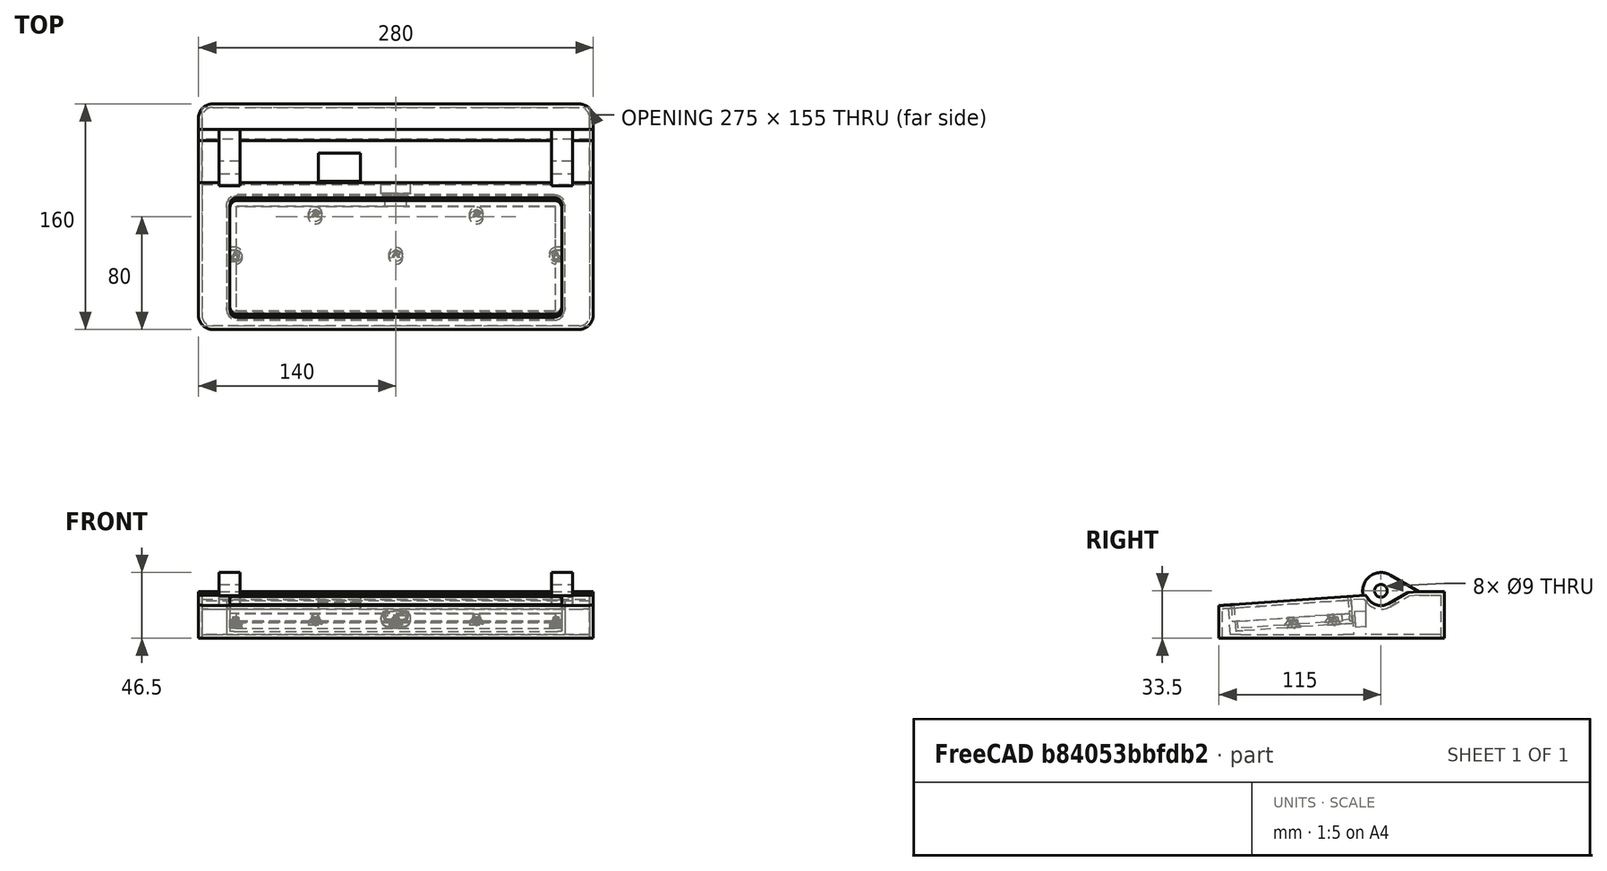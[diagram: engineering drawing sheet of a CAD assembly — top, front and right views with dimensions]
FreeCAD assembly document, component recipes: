
FREECAD ASSEMBLY — COMPONENT RECIPES ("BottomEnclosure_v3")

This assembly document has 6 components, labeled P0..P5 below (a component is one placed body or linked part). 5 of them carry a construction recipe — the FreeCAD feature program that regenerates the part from scratch, quoted from this document or its linked companion documents; the rest are supplied as boundary geometry only. No exploded tour is included for this assembly.
COMPONENT P0 — recipe-attached ("Bottom Enclosure - 0", modeled in this document).
Construction recipe (the document's own serialized feature program — sketch geometry with constraints, then the solid features built on it; lengths are millimeters unless a unit is written):

FEATURE [PartDesign::Boolean] Boolean
  Group = -> [Binder]
  Refine = true
  Suppressed = false
  Type = 0
  UsePlacement = true
FEATURE [PartDesign::SubShapeBinder] Binder011
  BindCopyOnChange = 0
  BindMode = 0
  ClaimChildren = false
  Context = -> Body [Binder011.]
  Fuse = false
  MakeFace = false
  OffsetFill = false
  OffsetIntersection = false
  OffsetJoinType = 0
  OffsetOpenResult = false
  PartialLoad = false
  Placement = pos=(-3.64e-14,-49.9267,26.5088) rot=(1,0,0;0.069813rad)
  Refine = true
  Relative = true
  Support = -> [Link001,Link002]
  _Version = 2
  expr: .Placement.Rotation.Angle = <<Vars>>.hood_angle
FEATURE [PartDesign::SubShapeBinder] Binder018
  BindCopyOnChange = 0
  BindMode = 0
  ClaimChildren = false
  Context = -> Body [Binder018.]
  Fuse = false
  MakeFace = true
  Offset = 2.5
  OffsetFill = false
  OffsetIntersection = false
  OffsetJoinType = 2
  OffsetOpenResult = false
  PartialLoad = false
  Refine = true
  Relative = true
  Support = -> [Binder011[Edge14,Edge13,Edge12,Edge11,Edge7,Edge8,Edge9,Edge10]]
  _Version = 2
  expr: Offset = <<Vars>>.wall
FEATURE [PartDesign::Pad] Pad
  BaseFeature = -> Boolean
  Direction = (0,-0.0697565,0.997564)
  Length = 10
  Length2 = 10
  Offset = -2.5
  Profile = -> Binder018
  Refine = true
  Suppressed = false
  Type = 3
  UpToFace = -> Boolean [Face12]
  expr: Offset = -<<Vars>>.wall
FEATURE [PartDesign::SubShapeBinder] Binder019
  BindCopyOnChange = 0
  BindMode = 0
  ClaimChildren = false
  Context = -> Body [Binder019.]
  Fuse = false
  MakeFace = true
  Offset = 0.2
  OffsetFill = false
  OffsetIntersection = false
  OffsetJoinType = 2
  OffsetOpenResult = false
  PartialLoad = false
  Refine = true
  Relative = true
  Support = -> [Binder011[Edge7,Edge14,Edge13,Edge12,Edge11,Edge10,Edge9,Edge8]]
  _Version = 2
  expr: Offset = <<Vars>>.clearance
FEATURE [PartDesign::Pocket] Pocket
  BaseFeature = -> Pad
  Direction = (0,0.0697565,-0.997564)
  Length = 12
  Length2 = 5
  Profile = -> Binder019
  Refine = true
  Suppressed = false
  Type = 0
FEATURE [PartDesign::SubShapeBinder] Binder020
  BindCopyOnChange = 0
  BindMode = 0
  ClaimChildren = false
  Context = -> Body [Binder020.]
  Fuse = false
  MakeFace = true
  Offset = -1
  OffsetFill = false
  OffsetIntersection = false
  OffsetJoinType = 0
  OffsetOpenResult = false
  PartialLoad = false
  Placement = pos=(0,0,-12) rot=(0,0,1;0rad)
  Refine = true
  Relative = true
  Support = -> [Binder011[Edge16,Edge15,Edge18,Edge17]]
  _Version = 2
FEATURE [PartDesign::Pocket] Pocket005
  BaseFeature = -> Pocket
  Direction = (0,0.0697565,-0.997564)
  Length = 5
  Length2 = 5
  Profile = -> Binder020
  Refine = true
  Suppressed = false
  Type = 0
FEATURE [Sketcher::SketchObject] Sketch014  label="Sketch015"
  ArcFitTolerance = 1e-06
  AttachmentSupport = -> [Pocket005]
  ExternalGeometry = -> [Binder011]
  FullyConstrained = true
  MakeInternals = false
  MapMode = 5
  Placement = pos=(0,-0.903776,12.9246) rot=(1,0,0;0.069813rad)
  sketch-geometry (5):
    g0: Circle CenterX=-113.798 CenterY=-47.9567 CenterZ=0 NormalX=0 NormalY=0 NormalZ=1 AngleXU=0 Radius=2.5
    g1: Circle CenterX=-57.1492 CenterY=-19.3809 CenterZ=0 NormalX=0 NormalY=0 NormalZ=1 AngleXU=0 Radius=2.5
    g2: Circle CenterX=-3.64e-14 CenterY=-47.9559 CenterZ=0 NormalX=0 NormalY=0 NormalZ=1 AngleXU=0 Radius=2.5
    g3: Circle CenterX=57.151 CenterY=-19.3809 CenterZ=0 NormalX=0 NormalY=0 NormalZ=1 AngleXU=0 Radius=2.5
    g4: Circle CenterX=113.801 CenterY=-47.9567 CenterZ=0 NormalX=0 NormalY=0 NormalZ=1 AngleXU=0 Radius=2.5
  constraints (10):
    c: Coincident(g0,g-4)
    c: Coincident(g1,g-3)
    c: Coincident(g2,g-5)
    c: Coincident(g3,g-6)
    c: Coincident(g4,g-7)
    c: Equal(g4,g3)
    c: Equal(g3,g2)
    c: Equal(g2,g1)
    c: Equal(g1,g0)
    c: Diameter(g2) = 5
FEATURE [PartDesign::Pad] Pad003
  BaseFeature = -> Pocket005
  Direction = (0,-0.0697565,0.997564)
  Length = 5
  Length2 = 10
  Profile = -> Sketch014
  ReferenceAxis = -> Sketch014 [N_Axis]
  Refine = true
  Suppressed = false
  Type = 0
FEATURE [PartDesign::Chamfer] Chamfer
  Angle = 45
  Base = -> Pad003 [Edge215,Edge233,Edge232,Edge231,Edge225]
  BaseFeature = -> Pad003
  ChamferType = 0
  FlipDirection = false
  Refine = true
  Size = 2.5
  Size2 = 1
  SupportTransform = false
  Suppressed = false
  UseAllEdges = false
FEATURE [PartDesign::Hole] Hole
  BaseFeature = -> Chamfer
  CustomThreadClearance = 0
  Depth = 4
  DepthType = 0
  Diameter = 3
  DrillForDepth = false
  DrillPoint = 1
  DrillPointAngle = 118
  HoleCutCountersinkAngle = 90
  HoleCutCustomValues = false
  HoleCutDepth = 0
  HoleCutDiameter = 6.1
  HoleCutType = 0
  ModelThread = false
  Profile = -> Chamfer [Edge10,Edge87,Edge89,Edge91,Edge64]
  Refine = true
  Suppressed = false
  Tapered = false
  TaperedAngle = 90
  ThreadClass = 0
  ThreadDepth = 4
  ThreadDepthType = 0
  ThreadDirection = 0
  ThreadFit = 0
  ThreadSize = 0
  ThreadType = 0
  Threaded = false
  UseCustomThreadClearance = false
  expr: Diameter = <<Vars>>.nut_inserts_m2
FEATURE [Sketcher::SketchObject] Sketch015  label="Sketch016"
  ArcFitTolerance = 1e-06
  AttachmentSupport = -> [Hole]
  ExternalGeometry = -> [Hole]
  FullyConstrained = true
  MakeInternals = false
  MapMode = 5
  Placement = pos=(0,-6.49004,-0.453828) rot=(1,0,0;1.64061rad)
  sketch-geometry (8):
    g0: LineSegment StartX=-7.5 StartY=17.9269 StartZ=0 EndX=-7.5 EndY=15.9269 EndZ=0
    g1: LineSegment StartX=-5.5 StartY=13.9269 StartZ=0 EndX=5.5 EndY=13.9269 EndZ=0
    g2: LineSegment StartX=7.5 StartY=15.9269 StartZ=0 EndX=7.5 EndY=17.9269 EndZ=0
    g3: LineSegment StartX=7.5 StartY=17.9269 StartZ=0 EndX=-7.5 EndY=17.9269 EndZ=0
    g4: ArcOfCircle CenterX=-5.5 CenterY=15.9269 CenterZ=0 NormalX=0 NormalY=0 NormalZ=1 AngleXU=0 Radius=2 StartAngle=3.14159 EndAngle=4.71239
    g5: GeomPoint [constr] X=-7.5 Y=13.9269 Z=0
    g6: ArcOfCircle CenterX=5.5 CenterY=15.9269 CenterZ=0 NormalX=0 NormalY=0 NormalZ=1 AngleXU=0 Radius=2 StartAngle=4.71239 EndAngle=6.28319
    g7: GeomPoint [constr] X=7.5 Y=13.9269 Z=0
  constraints (19):
    c: Coincident(g2,g3)
    c: Coincident(g3,g0)
    c: Vertical(g0)
    c: Vertical(g2)
    c: Horizontal(g1)
    c: Symmetric(g0,g2,g-2)
    c: DistanceX(g3,g3) = 15
    c: DistanceY(g7,g2) = 4
    c: PointOnObject(g0,g-3)
    c: PointOnObject(g5,g0)
    c: PointOnObject(g5,g1)
    c: Tangent(g0,g4) = -1.5708
    c: Tangent(g1,g4) = -1.5708
    c: PointOnObject(g7,g1)
    c: PointOnObject(g7,g2)
    c: Tangent(g1,g6) = -1.5708
    c: Tangent(g2,g6) = -1.5708
    c: Equal(g6,g4)
    c: Radius(g6) = 2
FEATURE [PartDesign::Pocket] Pocket006
  BaseFeature = -> Hole
  Direction = (0,0.997564,0.0697565)
  Length = 20
  Length2 = 5
  Midplane = true
  Profile = -> Sketch015
  ReferenceAxis = -> Sketch015 [N_Axis]
  Refine = true
  Suppressed = false
  Type = 0
FEATURE [PartDesign::SubShapeBinder] Binder021
  BindCopyOnChange = 0
  BindMode = 0
  ClaimChildren = false
  Context = -> Body [Binder021.]
  Fuse = false
  MakeFace = true
  Offset = 1.5
  OffsetFill = false
  OffsetIntersection = false
  OffsetJoinType = 2
  OffsetOpenResult = false
  PartialLoad = false
  Refine = true
  Relative = true
  Support = -> [Pocket006[Edge110,Edge69,Edge93,Edge91,Edge89,Edge80]]
  _Version = 2
FEATURE [PartDesign::Pocket] Pocket007
  BaseFeature = -> Pocket006
  Direction = (0,-0.997564,-0.0697565)
  Length = 2
  Length2 = 5
  Profile = -> Binder021
  Refine = true
  Suppressed = false
  Type = 0
FEATURE [PartDesign::Body] Body  label="Bottom Enclosure - 0"
  AllowCompound = false
  Group = -> [Boolean,Binder011,Binder018,Pad,Binder019,Pocket,Binder020,Pocket005,Sketch014,Pad003,Chamfer,Hole,Sketch015,Pocket006,Binder021,Pocket007]
  Origin = -> Origin
  Tip = -> Pocket007
COMPONENT P1 — recipe-attached ("Bottom Enclosure - Base", modeled in this document).
Construction recipe (the document's own serialized feature program — sketch geometry with constraints, then the solid features built on it; lengths are millimeters unless a unit is written):

FEATURE [Sketcher::SketchObject] Sketch008
  ArcFitTolerance = 1e-06
  AttachmentSupport = -> [YZ_Plane002]
  FullyConstrained = true
  MakeInternals = false
  MapMode = 5
  Placement = pos=(0,0,0) rot=(0.57735,0.57735,0.57735;2.0944rad)
  expr: Constraints[15] = <<Vars>>.hood_angle
  expr: Constraints[16] = <<Vars>>.bottom_enclosure_height
  expr: Constraints[8] = <<Vars>>.top_enclosure_height
  expr: Constraints[9] = <<Vars>>.bottom_enclosure_depth
  sketch-geometry (12):
    g0: LineSegment StartX=-100 StartY=0 StartZ=0 EndX=-100 EndY=23.0073 EndZ=0
    g1: LineSegment StartX=-100 StartY=23.0073 StartZ=0 EndX=0 EndY=30 EndZ=0
    g2: LineSegment StartX=60 StartY=32.9354 StartZ=0 EndX=60 EndY=0 EndZ=0
    g3: LineSegment StartX=60 StartY=0 StartZ=0 EndX=-100 EndY=0 EndZ=0
    g4: LineSegment [constr] StartX=0 StartY=30 StartZ=0 EndX=-100 EndY=30 EndZ=0
    g5: LineSegment [constr] StartX=-100 StartY=30 StartZ=0 EndX=-100 EndY=23.0073 EndZ=0
    g6: LineSegment [constr] StartX=41.9779 StartY=32.9354 StartZ=0 EndX=21.5 EndY=44.7583 EndZ=0
    g7: LineSegment StartX=0 StartY=30 StartZ=0 EndX=41.9779 EndY=32.9354 EndZ=0
    g8: LineSegment StartX=41.9779 StartY=32.9354 StartZ=0 EndX=60 EndY=32.9354 EndZ=0
    g9: Circle CenterX=15 CenterY=33.5 CenterZ=0 NormalX=0 NormalY=0 NormalZ=1 AngleXU=0 Radius=4.5
    g10: Circle CenterX=15 CenterY=33.5 CenterZ=0 NormalX=0 NormalY=0 NormalZ=1 AngleXU=0 Radius=10
    g11: LineSegment [constr] StartX=15 StartY=33.5 StartZ=0 EndX=21.5 EndY=44.7583 EndZ=0
  constraints (33):
    c: PointOnObject(g0,g-1)
    c: Vertical(g0)
    c: Coincident(g0,g1)
    c: PointOnObject(g1,g-2)
    c: PointOnObject(g2,g-1)
    c: Vertical(g2)
    c: Coincident(g2,g3)
    c: Coincident(g3,g0)
    c: DistanceX(g0,g-1) = 100
    c: DistanceY(g0,g1) = 30
    c: Coincident(g1,g4)
    c: Horizontal(g4)
    c: Coincident(g4,g5)
    c: Coincident(g5,g0)
    c: Vertical(g5)
    c: Angle(g4,g1) = 0.0698132
    c: DistanceX(g0,g2) = 160
    c: Angle(g6,g-1) = 0.523599
    c: Coincident(g7,g1)
    c: Coincident(g7,g6)
    c: Coincident(g8,g6)
    c: Coincident(g8,g2)
    c: Horizontal(g8)
    c: Parallel(g1,g7)
    c: DistanceX(g-1,g9) = 15
    c: Diameter(g9) = 9
    c: DistanceY(g-1,g9) = 33.5
    c: Coincident(g10,g9)
    c: Diameter(g10) = 20
    c: Coincident(g11,g9)
    c: Coincident(g6,g11)
    c: Perpendicular(g6,g11)
    c: Distance(g11) = 13
FEATURE [Sketcher::SketchObject] Sketch
  ArcFitTolerance = 1e-06
  AttachmentSupport = -> [YZ_Plane002]
  ExternalGeometry = -> [Sketch008]
  FullyConstrained = true
  MakeInternals = false
  MapMode = 5
  Placement = pos=(0,0,0) rot=(0.57735,0.57735,0.57735;2.0944rad)
  sketch-geometry (6):
    g0: ArcOfCircle CenterX=15 CenterY=33.5 CenterZ=0 NormalX=0 NormalY=0 NormalZ=1 AngleXU=0 Radius=10.5 StartAngle=3.83972 EndAngle=5.23599
    g1: LineSegment StartX=3.99563 StartY=30.2794 StartZ=0 EndX=6.95653 EndY=26.7507 EndZ=0
    g2: LineSegment StartX=20.25 StartY=24.4067 StartZ=0 EndX=34.0635 EndY=32.382 EndZ=0
    g3: LineSegment [constr] StartX=6.95653 StartY=26.7507 StartZ=0 EndX=7.33956 EndY=27.0721 EndZ=0
    g4: LineSegment [constr] StartX=7.33956 StartY=27.0721 StartZ=0 EndX=15 EndY=33.5 EndZ=0
    g5: LineSegment StartX=3.99563 StartY=30.2794 StartZ=0 EndX=34.0635 EndY=32.382 EndZ=0
  constraints (15):
    c: Coincident(g0,g-3)
    c: PointOnObject(g1,g-5)
    c: Coincident(g3,g1)
    c: Coincident(g4,g0)
    c: PointOnObject(g2,g-5)
    c: Angle(g-1,g2) = 0.523599
    c: Tangent(g0,g1) = -1.5708
    c: Tangent(g0,g2) = -1.5708
    c: Coincident(g3,g4)
    c: PointOnObject(g3,g-4)
    c: Parallel(g3,g4)
    c: Coincident(g5,g1)
    c: Coincident(g5,g2)
    c: Angle(g-1,g4) = 0.698132
    c: Distance(g0,g3) = 0.5
FEATURE [Sketcher::SketchObject] Sketch012  label="Sketch013"
  ArcFitTolerance = 1e-06
  AttachmentSupport = -> [YZ_Plane002]
  ExternalGeometry = -> [Sketch,Sketch008]
  FullyConstrained = true
  MakeInternals = false
  MapMode = 5
  Placement = pos=(0,0,0) rot=(0.57735,0.57735,0.57735;2.0944rad)
  sketch-geometry (7):
    g0: ArcOfCircle CenterX=15 CenterY=33.5 CenterZ=0 NormalX=0 NormalY=0 NormalZ=1 AngleXU=0 Radius=13 StartAngle=1.0472 EndAngle=3.40062
    g1: LineSegment StartX=21.5 StartY=44.7583 StartZ=0 EndX=41.9779 EndY=32.9354 EndZ=0
    g2: LineSegment StartX=2.43368 StartY=30.1702 StartZ=0 EndX=3.99563 EndY=30.2794 EndZ=0
    g3: LineSegment StartX=34.0635 StartY=32.382 StartZ=0 EndX=41.9779 EndY=32.9354 EndZ=0
    g4: LineSegment StartX=3.99563 StartY=30.2794 StartZ=0 EndX=6.95653 EndY=26.7507 EndZ=0
    g5: LineSegment StartX=20.25 StartY=24.4067 StartZ=0 EndX=34.0635 EndY=32.382 EndZ=0
    g6: ArcOfCircle CenterX=15 CenterY=33.5 CenterZ=0 NormalX=0 NormalY=0 NormalZ=1 AngleXU=0 Radius=10.5 StartAngle=3.83972 EndAngle=5.23599
  constraints (16):
    c: Diameter(g0) = 26
    c: Coincident(g0,g-3)
    c: Coincident(g1,g-6)
    c: Tangent(g0,g1) = 1.5708
    c: PointOnObject(g0,g-6)
    c: Coincident(g2,g0)
    c: Coincident(g2,g-4)
    c: Coincident(g3,g-5)
    c: Coincident(g3,g1)
    c: Coincident(g4,g2)
    c: Coincident(g4,g-4)
    c: Coincident(g5,g-5)
    c: Coincident(g5,g3)
    c: Coincident(g6,g4)
    c: Coincident(g6,g5)
    c: Tangent(g6,g-3)
FEATURE [PartDesign::SubShapeBinder] Binder014
  BindCopyOnChange = 0
  BindMode = 0
  ClaimChildren = false
  Context = -> Body002 [Binder014.]
  Fuse = false
  MakeFace = true
  OffsetFill = false
  OffsetIntersection = false
  OffsetJoinType = 0
  OffsetOpenResult = false
  PartialLoad = false
  Refine = true
  Relative = true
  Support = -> [Sketch008[Edge2,Edge3,Edge4,Edge5,Edge6,Edge1]]
  _Version = 2
FEATURE [PartDesign::SubShapeBinder] Binder015
  BindCopyOnChange = 0
  BindMode = 0
  ClaimChildren = false
  Context = -> Body002 [Binder015.]
  Fuse = false
  MakeFace = true
  OffsetFill = false
  OffsetIntersection = false
  OffsetJoinType = 0
  OffsetOpenResult = false
  PartialLoad = false
  Refine = true
  Relative = true
  Support = -> [Sketch]
  _Version = 2
FEATURE [PartDesign::SubShapeBinder] Binder016
  BindCopyOnChange = 0
  BindMode = 0
  ClaimChildren = false
  Context = -> Body002 [Binder016.]
  Fuse = false
  MakeFace = true
  OffsetFill = false
  OffsetIntersection = false
  OffsetJoinType = 0
  OffsetOpenResult = false
  PartialLoad = false
  Placement = pos=(110.4,0,0) rot=(0,0,1;0rad)
  Refine = true
  Relative = true
  Support = -> [Sketch012]
  _Version = 2
  expr: .Placement.Base.x = (<<Vars>>.top_enclosure_width - 32 * 2) / 2 + 2.4
FEATURE [PartDesign::SubShapeBinder] Binder017
  BindCopyOnChange = 0
  BindMode = 0
  ClaimChildren = false
  Context = -> Body002 [Binder017.]
  Fuse = false
  MakeFace = true
  OffsetFill = false
  OffsetIntersection = false
  OffsetJoinType = 0
  OffsetOpenResult = false
  PartialLoad = false
  Refine = true
  Relative = true
  Support = -> [Sketch008[Edge7]]
  _Version = 2
FEATURE [PartDesign::Pad] Pad001
  Direction = (1,0,0)
  Length = 280
  Length2 = 10
  Midplane = true
  Profile = -> Binder014
  Refine = true
  Suppressed = false
  Type = 0
  expr: Length = <<Vars>>.top_enclosure_width
FEATURE [PartDesign::Fillet] Fillet
  Base = -> Pad001 [Edge12,Edge13,Edge7,Edge6]
  BaseFeature = -> Pad001
  Radius = 10
  Refine = true
  SupportTransform = false
  Suppressed = false
  UseAllEdges = false
  expr: Radius = <<Vars>>.ext_radius
FEATURE [PartDesign::Pocket] Pocket001
  BaseFeature = -> Fillet
  Direction = (-1,0,0)
  Length = 5
  Length2 = 5
  Midplane = true
  Profile = -> Binder015
  Refine = true
  Suppressed = false
  Type = 1
FEATURE [PartDesign::Thickness] Thickness
  Base = -> Pocket001 [Face8]
  BaseFeature = -> Pocket001
  Intersection = true
  Join = 1
  Mode = 0
  Refine = true
  Reversed = true
  SupportTransform = false
  Suppressed = false
  Value = 2.5
  expr: Value = <<Vars>>.wall
FEATURE [PartDesign::Pad] Pad002
  BaseFeature = -> Thickness
  Direction = (1,0,0)
  Length = 15
  Length2 = 10
  Profile = -> Binder016
  Refine = true
  Suppressed = false
  Type = 0
FEATURE [PartDesign::Mirrored] Mirrored
  BaseFeature = -> Pad002
  MirrorPlane = -> YZ_Plane002
  Originals = -> [Pad002]
  Refine = true
  Suppressed = false
  TransformMode = 0
FEATURE [PartDesign::Pocket] Pocket002
  BaseFeature = -> Mirrored
  Direction = (-1,0,0)
  Length = 5
  Length2 = 5
  Midplane = true
  Profile = -> Binder017
  Refine = true
  Suppressed = false
  Type = 1
FEATURE [Sketcher::SketchObject] Sketch013  label="Sketch014"
  ArcFitTolerance = 1e-06
  AttachmentSupport = -> [XY_Plane002]
  FullyConstrained = true
  MakeInternals = false
  MapMode = 5
  expr: Constraints[10] = <<Vars>>.wire_hole_offset_x
  expr: Constraints[9] = <<Vars>>.wire_hole_width
  sketch-geometry (5):
    g0: LineSegment StartX=-55 StartY=5 StartZ=0 EndX=-25 EndY=5 EndZ=0
    g1: LineSegment StartX=-25 StartY=5 StartZ=0 EndX=-25 EndY=25 EndZ=0
    g2: LineSegment StartX=-25 StartY=25 StartZ=0 EndX=-55 EndY=25 EndZ=0
    g3: LineSegment StartX=-55 StartY=25 StartZ=0 EndX=-55 EndY=5 EndZ=0
    g4: GeomPoint [constr] X=-40 Y=15 Z=0
  constraints (13):
    c: Coincident(g0,g1)
    c: Coincident(g1,g2)
    c: Coincident(g2,g3)
    c: Coincident(g3,g0)
    c: Horizontal(g0)
    c: Horizontal(g2)
    c: Vertical(g1)
    c: Vertical(g3)
    c: Symmetric(g2,g0,g4)
    c: DistanceX(g2,g2) = 30
    c: DistanceX(g4,g-1) = 40
    c: DistanceY(g-1,g4) = 15
    c: DistanceY(g3,g3) = 20
FEATURE [PartDesign::Pocket] Pocket003
  BaseFeature = -> Pocket002
  Direction = (0,0,-1)
  Length = 5
  Length2 = 5
  Midplane = true
  Profile = -> Sketch013
  ReferenceAxis = -> Sketch013 [N_Axis]
  Refine = true
  Suppressed = false
  Type = 1
FEATURE [PartDesign::Body] Body002  label="Bottom Enclosure - Base"
  AllowCompound = false
  Group = -> [Sketch008,Sketch,Sketch012,Binder014,Binder015,Binder016,Binder017,Pad001,Fillet,Pocket001,Thickness,Pad002,Mirrored,Pocket002,Sketch013,Pocket003]
  Origin = -> Origin002
  Tip = -> Pocket003
COMPONENT P2 — recipe-attached ("Bottom Enclosure - 0.1", modeled in this document).
Construction recipe (the document's own serialized feature program — sketch geometry with constraints, then the solid features built on it; lengths are millimeters unless a unit is written):

FEATURE [PartDesign::Boolean] Boolean001
  Group = -> [Binder022]
  Refine = true
  Suppressed = false
  Type = 0
  UsePlacement = true
FEATURE [Sketcher::SketchObject] Sketch016  label="Sketch017"
  ArcFitTolerance = 1e-06
  AttachmentSupport = -> [XY_Plane003]
  ExternalGeometry = -> [Boolean001]
  FullyConstrained = true
  MakeInternals = false
  MapMode = 5
  sketch-geometry (8):
    g0: LineSegment StartX=-140 StartY=3.99563 StartZ=0 EndX=-140 EndY=-90 EndZ=0
    g1: LineSegment StartX=-130 StartY=-100 StartZ=0 EndX=130 EndY=-100 EndZ=0
    g2: LineSegment StartX=140 StartY=-90 StartZ=0 EndX=140 EndY=3.99563 EndZ=0
    g3: LineSegment StartX=140 StartY=3.99563 StartZ=0 EndX=-140 EndY=3.99563 EndZ=0
    g4: ArcOfCircle CenterX=-130 CenterY=-90 CenterZ=0 NormalX=0 NormalY=0 NormalZ=1 AngleXU=0 Radius=10 StartAngle=3.14159 EndAngle=4.71239
    g5: GeomPoint [constr] X=-140 Y=-100 Z=0
    g6: ArcOfCircle CenterX=130 CenterY=-90 CenterZ=0 NormalX=0 NormalY=0 NormalZ=1 AngleXU=0 Radius=10 StartAngle=4.71239 EndAngle=6.28319
    g7: GeomPoint [constr] X=140 Y=-100 Z=0
  constraints (18):
    c: Coincident(g2,g3)
    c: Coincident(g3,g0)
    c: Vertical(g0)
    c: Vertical(g2)
    c: Horizontal(g1)
    c: Horizontal(g3)
    c: PointOnObject(g-4,g1)
    c: PointOnObject(g-3,g3)
    c: PointOnObject(g5,g0)
    c: PointOnObject(g5,g1)
    c: Tangent(g0,g4) = -1.5708
    c: Tangent(g1,g4) = -1.5708
    c: PointOnObject(g7,g1)
    c: PointOnObject(g7,g2)
    c: Tangent(g1,g6) = -1.5708
    c: Tangent(g2,g6) = -1.5708
    c: Coincident(g-5,g2)
    c: Coincident(g0,g-6)
FEATURE [PartDesign::Pad] Pad004
  BaseFeature = -> Boolean001
  Direction = (0,0,1)
  Length = 10
  Length2 = 10
  Profile = -> Sketch016
  ReferenceAxis = -> Sketch016 [N_Axis]
  Refine = true
  Suppressed = false
  Type = 2
FEATURE [PartDesign::SubShapeBinder] Binder023
  BindCopyOnChange = 0
  BindMode = 0
  ClaimChildren = false
  Context = -> Body003 [Binder023.]
  Fuse = false
  MakeFace = true
  OffsetFill = false
  OffsetIntersection = false
  OffsetJoinType = 0
  OffsetOpenResult = false
  PartialLoad = false
  Refine = true
  Relative = true
  Support = -> [Pad004[Edge17,Edge13,Edge15,Edge135,Edge141,Edge140,Edge139,Edge138]]
  _Version = 2
FEATURE [PartDesign::Pad] Pad005
  BaseFeature = -> Pad004
  Direction = (0,0,1)
  Length = 2.5
  Length2 = 10
  Profile = -> Binder023
  Refine = true
  Suppressed = false
  Type = 0
  expr: Length = <<Vars>>.wall
FEATURE [PartDesign::Body] Body003  label="Bottom Enclosure - 0.1"
  AllowCompound = false
  Group = -> [Boolean001,Sketch016,Pad004,Binder023,Pad005]
  Origin = -> Origin003
  Tip = -> Pad005
COMPONENT P3 — recipe-attached ("Bottom Enclosure - 1", modeled in this document).
Construction recipe (the document's own serialized feature program — sketch geometry with constraints, then the solid features built on it; lengths are millimeters unless a unit is written):

FEATURE [PartDesign::Boolean] Boolean002
  Group = -> [Binder024]
  Refine = true
  Suppressed = false
  Type = 0
  UsePlacement = true
FEATURE [PartDesign::SubShapeBinder] Binder025
  BindCopyOnChange = 0
  BindMode = 0
  ClaimChildren = false
  Context = -> Body004 [Binder025.]
  Fuse = false
  MakeFace = false
  OffsetFill = false
  OffsetIntersection = false
  OffsetJoinType = 0
  OffsetOpenResult = false
  PartialLoad = false
  Placement = pos=(2.81e-14,-48.0113,26.6427) rot=(1,0,0;0.069813rad)
  Refine = true
  Relative = true
  Support = -> [Link001,Link002]
  _Version = 2
  expr: .Placement.Rotation.Angle = <<Vars>>.hood_angle
FEATURE [PartDesign::SubShapeBinder] Binder026
  BindCopyOnChange = 0
  BindMode = 0
  ClaimChildren = false
  Context = -> Body004 [Binder026.]
  Fuse = false
  MakeFace = true
  Offset = 0.2
  OffsetFill = false
  OffsetIntersection = false
  OffsetJoinType = 2
  OffsetOpenResult = false
  PartialLoad = false
  Refine = true
  Relative = true
  Support = -> [Binder025[Edge7,Edge14,Edge13,Edge12,Edge11,Edge10,Edge9,Edge8]]
  _Version = 2
  expr: Offset = <<Vars>>.clearance
FEATURE [PartDesign::Pocket] Pocket008
  BaseFeature = -> Boolean002
  Direction = (0,0.0697565,-0.997564)
  Length = 19
  Length2 = 5
  Profile = -> Binder026
  Refine = true
  Suppressed = false
  Type = 0
  expr: Length = 19 mm
FEATURE [Sketcher::SketchObject] Sketch017  label="Sketch018"
  ArcFitTolerance = 1e-06
  AttachmentSupport = -> [Pocket008]
  ExternalGeometry = -> [Binder025]
  FullyConstrained = true
  MakeInternals = false
  MapMode = 5
  Placement = pos=(0,-0.762224,10.9003) rot=(1,0,0;0.069813rad)
  sketch-geometry (11):
    g0: ArcOfCircle CenterX=-113.798 CenterY=-46.0366 CenterZ=0 NormalX=0 NormalY=0 NormalZ=1 AngleXU=0 Radius=3 StartAngle=4.71239 EndAngle=7.85398
    g1: Circle CenterX=-57.1491 CenterY=-17.4608 CenterZ=0 NormalX=0 NormalY=0 NormalZ=1 AngleXU=0 Radius=3
    g2: Circle CenterX=0 CenterY=-46.0358 CenterZ=0 NormalX=0 NormalY=0 NormalZ=1 AngleXU=0 Radius=3
    g3: Circle CenterX=57.151 CenterY=-17.4608 CenterZ=0 NormalX=0 NormalY=0 NormalZ=1 AngleXU=0 Radius=3
    g4: ArcOfCircle CenterX=113.802 CenterY=-46.0366 CenterZ=0 NormalX=0 NormalY=0 NormalZ=1 AngleXU=0 Radius=3 StartAngle=1.5708 EndAngle=4.71239
    g5: LineSegment StartX=-123.798 StartY=-43.0366 StartZ=0 EndX=-123.798 EndY=-49.0366 EndZ=0
    g6: LineSegment StartX=-123.798 StartY=-49.0366 StartZ=0 EndX=-113.798 EndY=-49.0366 EndZ=0
    g7: LineSegment StartX=-113.798 StartY=-43.0366 StartZ=0 EndX=-123.798 EndY=-43.0366 EndZ=0
    g8: LineSegment StartX=113.802 StartY=-49.0366 StartZ=0 EndX=123.802 EndY=-49.0366 EndZ=0
    g9: LineSegment StartX=123.802 StartY=-49.0366 StartZ=0 EndX=123.802 EndY=-43.0366 EndZ=0
    g10: LineSegment StartX=123.802 StartY=-43.0366 StartZ=0 EndX=113.802 EndY=-43.0366 EndZ=0
  constraints (27):
    c: Coincident(g0,g-3)
    c: Coincident(g1,g-4)
    c: Coincident(g2,g-5)
    c: Coincident(g3,g-7)
    c: Coincident(g4,g-6)
    c: Equal(g4,g3)
    c: Equal(g3,g2)
    c: Coincident(g5,g6)
    c: Coincident(g7,g5)
    c: Vertical(g5)
    c: Horizontal(g7)
    c: DistanceX(g7,g7) = 10
    c: Tangent(g6,g0) = -1.5708
    c: Tangent(g0,g7) = -1.5708
    c: Horizontal(g6)
    c: Equal(g1,g0)
    c: Coincident(g8,g9)
    c: Coincident(g9,g10)
    c: Vertical(g9)
    c: Horizontal(g8)
    c: Coincident(g4,g10)
    c: Tangent(g4,g8) = -1.5708
    c: DistanceX(g10,g10) = 10
    c: Equal(g2,g1)
    c: Diameter(g2) = 6
    c: Vertical(g4,g4)
    c: Horizontal(g10)
FEATURE [PartDesign::Pad] Pad006
  BaseFeature = -> Pocket008
  Direction = (0,-0.0697565,0.997564)
  Length = 5
  Length2 = 10
  Profile = -> Sketch017
  ReferenceAxis = -> Sketch017 [N_Axis]
  Refine = true
  Suppressed = false
  Type = 0
FEATURE [PartDesign::Chamfer] Chamfer001
  Angle = 45
  Base = -> Pad006 [Edge148,Edge152,Edge151,Edge150,Edge145]
  BaseFeature = -> Pad006
  ChamferType = 0
  FlipDirection = false
  Refine = true
  Size = 2
  Size2 = 1
  SupportTransform = false
  Suppressed = false
  UseAllEdges = false
FEATURE [Sketcher::SketchObject] Sketch018  label="Sketch019"
  ArcFitTolerance = 1e-06
  AttachmentSupport = -> [Chamfer001]
  ExternalGeometry = -> [Binder025]
  FullyConstrained = true
  MakeInternals = false
  MapMode = 5
  Placement = pos=(0,-1.11101,15.8881) rot=(1,0,0;0.069813rad)
  sketch-geometry (5):
    g0: Circle CenterX=113.802 CenterY=-46.0366 CenterZ=0 NormalX=0 NormalY=0 NormalZ=1 AngleXU=0 Radius=1
    g1: Circle CenterX=57.151 CenterY=-17.4608 CenterZ=0 NormalX=0 NormalY=0 NormalZ=1 AngleXU=0 Radius=1
    g2: Circle CenterX=0 CenterY=-46.0358 CenterZ=0 NormalX=0 NormalY=0 NormalZ=1 AngleXU=0 Radius=1
    g3: Circle CenterX=-57.1491 CenterY=-17.4608 CenterZ=0 NormalX=0 NormalY=0 NormalZ=1 AngleXU=0 Radius=1
    g4: Circle CenterX=-113.798 CenterY=-46.0366 CenterZ=0 NormalX=0 NormalY=0 NormalZ=1 AngleXU=0 Radius=1
  constraints (10):
    c: Coincident(g0,g-7)
    c: Coincident(g1,g-6)
    c: Coincident(g2,g-5)
    c: Coincident(g3,g-4)
    c: Coincident(g4,g-3)
    c: Equal(g4,g3)
    c: Equal(g3,g2)
    c: Equal(g2,g1)
    c: Equal(g1,g0)
    c: Diameter(g2) = 2
FEATURE [PartDesign::Hole] Hole001
  BaseFeature = -> Chamfer001
  CustomThreadClearance = 0
  Depth = 5
  DepthType = 0
  Diameter = 3
  DrillForDepth = false
  DrillPoint = 1
  DrillPointAngle = 118
  HoleCutCountersinkAngle = 90
  HoleCutCustomValues = false
  HoleCutDepth = 0
  HoleCutDiameter = 6.1
  HoleCutType = 0
  ModelThread = false
  Profile = -> Sketch018
  Refine = true
  Suppressed = false
  Tapered = false
  TaperedAngle = 90
  ThreadClass = 0
  ThreadDepth = 5
  ThreadDepthType = 0
  ThreadDirection = 0
  ThreadFit = 0
  ThreadSize = 0
  ThreadType = 0
  Threaded = false
  UseCustomThreadClearance = false
  expr: Diameter = <<Vars>>.nut_inserts_m2
FEATURE [Sketcher::SketchObject] Sketch020  label="Sketch021"
  ArcFitTolerance = 1e-06
  AttachmentSupport = -> [Hole001]
  ExternalGeometry = -> [Hole001]
  FullyConstrained = false
  MakeInternals = false
  MapMode = 5
  Placement = pos=(0,-4.57466,-0.319891) rot=(1,0,0;1.64061rad)
  sketch-geometry (13):
    g0: LineSegment StartX=-5.5 StartY=11.2559 StartZ=0 EndX=5.5 EndY=11.2559 EndZ=0
    g1: LineSegment StartX=7.5 StartY=13.2559 StartZ=0 EndX=7.5 EndY=14.2559 EndZ=0
    g2: LineSegment StartX=5.5 StartY=16.2559 StartZ=0 EndX=-5.5 EndY=16.2559 EndZ=0
    g3: LineSegment StartX=-7.5 StartY=14.2559 StartZ=0 EndX=-7.5 EndY=13.2559 EndZ=0
    g4: GeomPoint [constr] X=0 Y=13.7559 Z=0
    g5: ArcOfCircle CenterX=5.5 CenterY=14.2559 CenterZ=0 NormalX=0 NormalY=0 NormalZ=1 AngleXU=0 Radius=2 StartAngle=2e-16 EndAngle=1.5708
    g6: GeomPoint [constr] X=7.5 Y=16.2559 Z=0
    g7: ArcOfCircle CenterX=5.5 CenterY=13.2559 CenterZ=0 NormalX=0 NormalY=0 NormalZ=1 AngleXU=0 Radius=2 StartAngle=4.71239 EndAngle=6.28319
    g8: GeomPoint [constr] X=7.5 Y=11.2559 Z=0
    g9: ArcOfCircle CenterX=-5.5 CenterY=13.2559 CenterZ=0 NormalX=0 NormalY=0 NormalZ=1 AngleXU=0 Radius=2 StartAngle=3.14159 EndAngle=4.71239
    g10: GeomPoint [constr] X=-7.5 Y=11.2559 Z=0
    g11: ArcOfCircle CenterX=-5.5 CenterY=14.2559 CenterZ=0 NormalX=0 NormalY=0 NormalZ=1 AngleXU=0 Radius=2 StartAngle=1.5708 EndAngle=3.14159
    g12: GeomPoint [constr] X=-7.5 Y=16.2559 Z=0
  constraints (28):
    c: Horizontal(g0)
    c: Horizontal(g2)
    c: Vertical(g1)
    c: Vertical(g3)
    c: Symmetric(g6,g10,g4)
    c: PointOnObject(g4,g-2)
    c: PointOnObject(g6,g1)
    c: PointOnObject(g6,g2)
    c: Tangent(g1,g5) = -1.5708
    c: Tangent(g2,g5) = -1.5708
    c: PointOnObject(g8,g0)
    c: PointOnObject(g8,g1)
    c: Tangent(g0,g7) = -1.5708
    c: Tangent(g1,g7) = -1.5708
    c: PointOnObject(g10,g0)
    c: PointOnObject(g10,g3)
    c: Tangent(g0,g9) = -1.5708
    c: Tangent(g3,g9) = -1.5708
    c: PointOnObject(g12,g2)
    c: PointOnObject(g12,g3)
    c: Tangent(g2,g11) = -1.5708
    c: Tangent(g3,g11) = -1.5708
    c: Equal(g9,g11)
    c: Equal(g11,g7)
    c: Equal(g7,g5)
    c: DistanceX(g3,g1) = 15
    c: DistanceY(g0,g2) = 5
    c: Radius(g11) = 2
FEATURE [PartDesign::Pocket] Pocket010
  BaseFeature = -> Hole001
  Direction = (0,0.997564,0.0697565)
  Length = 5
  Length2 = 5
  Profile = -> Sketch020
  ReferenceAxis = -> Sketch020 [N_Axis]
  Refine = true
  Suppressed = false
  Type = 2
FEATURE [PartDesign::SubShapeBinder] Binder028
  BindCopyOnChange = 0
  BindMode = 0
  ClaimChildren = false
  Context = -> Body004 [Binder028.]
  Fuse = false
  MakeFace = true
  Offset = 3
  OffsetFill = false
  OffsetIntersection = false
  OffsetJoinType = 2
  OffsetOpenResult = false
  PartialLoad = false
  Placement = pos=(0,2,0) rot=(0,0,1;0rad)
  Refine = true
  Relative = true
  Support = -> [Pocket010[Edge74,Edge75,Edge76,Edge77,Edge78,Edge79,Edge80,Edge73]]
  _Version = 2
FEATURE [PartDesign::Pocket] Pocket011
  BaseFeature = -> Pocket010
  Direction = (0,-0.997564,-0.0697565)
  Length = 5
  Length2 = 5
  Profile = -> Binder028
  Refine = true
  Reversed = true
  Suppressed = false
  Type = 2
FEATURE [PartDesign::Body] Body004  label="Bottom Enclosure - 1"
  AllowCompound = false
  Group = -> [Boolean002,Binder025,Binder026,Pocket008,Sketch017,Pad006,Chamfer001,Sketch018,Hole001,Sketch020,Pocket010,Binder028,Pocket011]
  Origin = -> Origin004
  Tip = -> Pocket011
COMPONENT P4 — recipe-attached ("Bottom Enclosure - 2", modeled in this document).
Construction recipe (the document's own serialized feature program — sketch geometry with constraints, then the solid features built on it; lengths are millimeters unless a unit is written):

FEATURE [PartDesign::Boolean] Boolean003
  Group = -> [Binder027]
  Refine = true
  Suppressed = false
  Type = 0
  UsePlacement = true
FEATURE [Sketcher::SketchObject] Sketch019  label="Sketch020"
  ArcFitTolerance = 1e-06
  AttachmentSupport = -> [Boolean003]
  ExternalGeometry = -> [Boolean003]
  FullyConstrained = true
  MakeInternals = false
  MapMode = 5
  Placement = pos=(0,60,0) rot=(0,0.707107,0.707107;3.14159rad)
  expr: Constraints[28] = <<Vars>>.ext_radius / 2
  expr: Constraints[29] = <<Vars>>.wall * 2
  expr: Constraints[30] = <<Vars>>.wall * 2
  sketch-geometry (14):
    g0: LineSegment StartX=-120 StartY=5 StartZ=0 EndX=120 EndY=5 EndZ=0
    g1: LineSegment StartX=125 StartY=10 StartZ=0 EndX=125 EndY=22.9354 EndZ=0
    g2: LineSegment StartX=120 StartY=27.9354 StartZ=0 EndX=-120 EndY=27.9354 EndZ=0
    g3: LineSegment StartX=-125 StartY=22.9354 StartZ=0 EndX=-125 EndY=10 EndZ=0
    g4: GeomPoint [constr] X=0 Y=16.4677 Z=0
    g5: LineSegment [constr] StartX=-130 StartY=16.4677 StartZ=0 EndX=130 EndY=16.4677 EndZ=0
    g6: ArcOfCircle CenterX=-120 CenterY=22.9354 CenterZ=0 NormalX=0 NormalY=0 NormalZ=1 AngleXU=0 Radius=5 StartAngle=1.5708 EndAngle=3.14159
    g7: GeomPoint [constr] X=-125 Y=27.9354 Z=0
    g8: ArcOfCircle CenterX=-120 CenterY=10 CenterZ=0 NormalX=0 NormalY=0 NormalZ=1 AngleXU=0 Radius=5 StartAngle=3.14159 EndAngle=4.71239
    g9: GeomPoint [constr] X=-125 Y=5 Z=0
    g10: ArcOfCircle CenterX=120 CenterY=22.9354 CenterZ=0 NormalX=0 NormalY=0 NormalZ=1 AngleXU=0 Radius=5 StartAngle=7e-16 EndAngle=1.5708
    g11: GeomPoint [constr] X=125 Y=27.9354 Z=0
    g12: ArcOfCircle CenterX=120 CenterY=10 CenterZ=0 NormalX=0 NormalY=0 NormalZ=1 AngleXU=0 Radius=5 StartAngle=4.71239 EndAngle=6.28319
    g13: GeomPoint [constr] X=125 Y=5 Z=0
  constraints (31):
    c: Horizontal(g0)
    c: Horizontal(g2)
    c: Vertical(g1)
    c: Vertical(g3)
    c: Symmetric(g11,g9,g4)
    c: PointOnObject(g4,g-2)
    c: Symmetric(g-3,g-3,g5)
    c: Symmetric(g-4,g-4,g5)
    c: PointOnObject(g4,g5)
    c: PointOnObject(g7,g2)
    c: PointOnObject(g7,g3)
    c: Tangent(g2,g6) = -1.5708
    c: Tangent(g3,g6) = -1.5708
    c: PointOnObject(g9,g0)
    c: PointOnObject(g9,g3)
    c: Tangent(g0,g8) = -1.5708
    c: Tangent(g3,g8) = -1.5708
    c: PointOnObject(g11,g1)
    c: PointOnObject(g11,g2)
    c: Tangent(g1,g10) = -1.5708
    c: Tangent(g2,g10) = -1.5708
    c: PointOnObject(g13,g0)
    c: PointOnObject(g13,g1)
    c: Tangent(g0,g12) = -1.5708
    c: Tangent(g1,g12) = -1.5708
    c: Equal(g6,g8)
    c: Equal(g8,g10)
    c: Equal(g10,g12)
    c: Radius(g6) = 5
    c: DistanceY(g7,g-3) = 5
    c: DistanceX(g-3,g7) = 5
FEATURE [Sketcher::SketchObject] Sketch021  label="Sketch022"
  ArcFitTolerance = 1e-06
  AttachmentSupport = -> [YZ_Plane005]
  ExternalGeometry = -> [Boolean003]
  FullyConstrained = true
  MakeInternals = false
  MapMode = 5
  Placement = pos=(0,0,0) rot=(0.57735,0.57735,0.57735;2.0944rad)
  sketch-geometry (8):
    g0: LineSegment StartX=3.99563 StartY=26.3901 StartZ=0 EndX=3.99563 EndY=2.5 EndZ=0
    g1: LineSegment StartX=3.99563 StartY=2.5 StartZ=0 EndX=57.5 EndY=2.5 EndZ=0
    g2: LineSegment StartX=57.5 StartY=2.5 StartZ=0 EndX=57.5 EndY=30.4354 EndZ=0
    g3: LineSegment StartX=57.5 StartY=30.4354 StartZ=0 EndX=42.0652 EndY=30.4354 EndZ=0
    g4: LineSegment StartX=42.0652 StartY=30.4354 StartZ=0 EndX=34.8136 EndY=29.9283 EndZ=0
    g5: LineSegment StartX=34.8136 StartY=29.9283 StartZ=0 EndX=21.5 EndY=22.2417 EndZ=0
    g6: LineSegment StartX=3.99563 StartY=26.3901 StartZ=0 EndX=5.04142 EndY=25.1438 EndZ=0
    g7: ArcOfCircle CenterX=15 CenterY=33.5 CenterZ=0 NormalX=0 NormalY=0 NormalZ=1 AngleXU=0 Radius=13 StartAngle=3.83972 EndAngle=5.23599
  constraints (16):
    c: Coincident(g-10,g0)
    c: Coincident(g0,g-10)
    c: Coincident(g0,g1)
    c: Coincident(g1,g-9)
    c: Coincident(g1,g2)
    c: Coincident(g2,g-9)
    c: Coincident(g2,g3)
    c: Coincident(g3,g-7)
    c: Coincident(g3,g4)
    c: Coincident(g6,g0)
    c: Coincident(g6,g-5)
    c: Coincident(g7,g-4)
    c: Coincident(g7,g6)
    c: Coincident(g5,g4)
    c: Coincident(g5,g-6)
    c: Tangent(g7,g5) = 1.5708
FEATURE [PartDesign::Body] Body005  label="Bottom Enclosure - 2"
  AllowCompound = false
  Group = -> [Boolean003,Sketch019,Sketch021]
  Origin = -> Origin005
  Tip = -> Boolean003
COMPONENT P5 — geometry summary ("Raspberry Pi Zero 2 W"; no construction recipe available for this part):
  bounding box: 65.8 x 30.6 x 5.1 mm
  tessellated surface: 68,994 triangles
  volume: 3703 mm^3 (36% of its bounding box)
PROVENANCE & LICENSES
A FreeCAD (.FCStd) document from a public repository crawl; recipes are the document's own serialized feature recipes (and, for linked parts, companion documents' recipes).
License: as declared in the source repository (recorded in the dataset sidecar).
